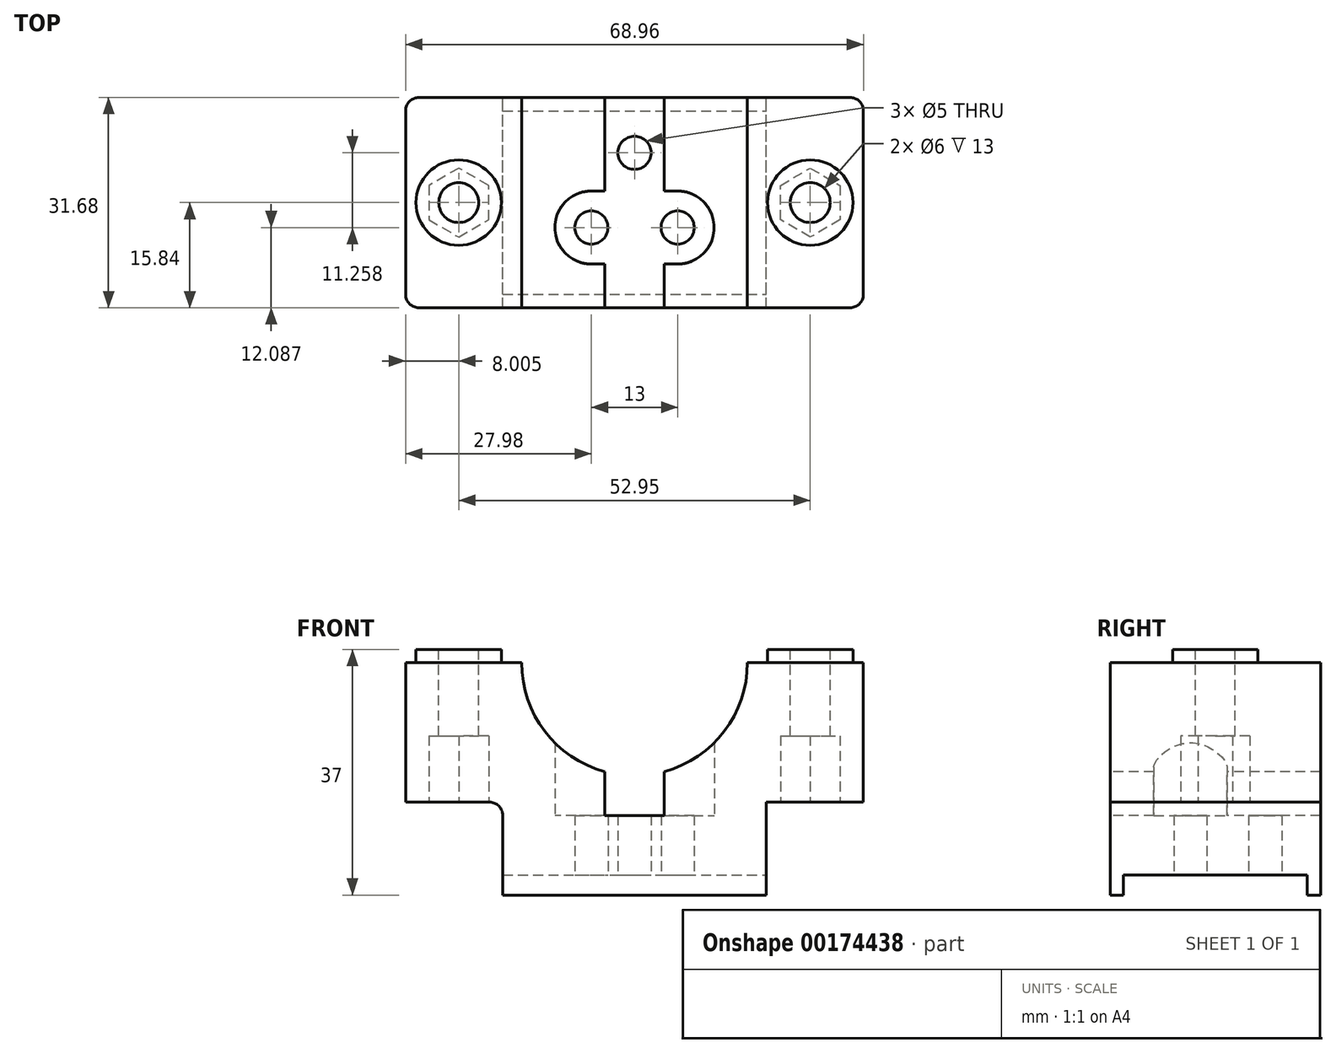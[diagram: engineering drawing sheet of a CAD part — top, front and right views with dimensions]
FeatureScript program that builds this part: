
annotation { "Feature Type Name" : "Feature", "Feature Type Description" : "" }
export const myFeature = defineFeature(function(context is Context, id is Id, definition is map)
    precondition{}
    {
        {
            var Q0;
            Q0=qCreatedBy(makeId("Top.planeOp"),FACE);
            var sketch = newSketch(context, id + "F0", { "sketchPlane" : qUnion([Q0])});
            skLineSegment(sketch, "E0.bottom", {"start": v(34.48, -15.84) * mm, "end": v(-34.48, -15.84) * mm});
            skLineSegment(sketch, "E0.top", {"start": v(34.48, 15.84) * mm, "end": v(-34.48, 15.84) * mm});
            skLineSegment(sketch, "E0.left", {"start": v(34.48, -15.84) * mm, "end": v(34.48, 15.84) * mm});
            skLineSegment(sketch, "E0.right", {"start": v(-34.48, -15.84) * mm, "end": v(-34.48, 15.84) * mm});
            skPoint(sketch, "E0.middle", {"position": v(0, 0) * mm});
            skSolve(sketch);
        }
        {
            var Q0;
            Q0 = qSketchRegion(id + "F0", true);
            extrude(context, id + "F1", {"entities" : qUnion([Q0]), "oppositeDirection" : true, "depth" : 21 * mm});
        }
        {
            var Q0;
            Q0=makeQuery(id+"F1.opExtrude","CAP_FACE",FACE,{"disambiguationData":[OSD([sQuery(id+"F0.wireOp",EDGE,"E0.bottom"),sQuery(id+"F0.wireOp",EDGE,"E0.top"),sQuery(id+"F0.wireOp",EDGE,"E0.left"),sQuery(id+"F0.wireOp",EDGE,"E0.right")])],"isStart":false});
            var sketch = newSketch(context, id + "F2", { "sketchPlane" : qUnion([Q0])});
            skLineSegment(sketch, "E1.bottom", {"start": v(19.85, 15.84) * mm, "end": v(-19.85, 15.84) * mm});
            skLineSegment(sketch, "E1.top", {"start": v(19.85, -15.84) * mm, "end": v(-19.85, -15.84) * mm});
            skLineSegment(sketch, "E1.left", {"start": v(19.85, 15.84) * mm, "end": v(19.85, -15.84) * mm});
            skLineSegment(sketch, "E1.right", {"start": v(-19.85, 15.84) * mm, "end": v(-19.85, -15.84) * mm});
            skPoint(sketch, "E1.middle", {"position": v(0, 0) * mm});
            skSolve(sketch);
        }
        {
            var Q0;
            Q0 = qSketchRegion(id + "F2", true);
            extrude(context, id + "F3", {"entities" : qUnion([Q0]), "operationType" : NewBodyOperationType.ADD, "depth" : 11 * mm});
        }
        {
            var Q0;
            Q0=makeQuery(id+"F1.opExtrude","CAP_FACE",FACE,{"disambiguationData":[OSD([sQuery(id+"F0.wireOp",EDGE,"E0.bottom"),sQuery(id+"F0.wireOp",EDGE,"E0.top"),sQuery(id+"F0.wireOp",EDGE,"E0.left"),sQuery(id+"F0.wireOp",EDGE,"E0.right")])],"isStart":true});
            var sketch = newSketch(context, id + "F4", { "sketchPlane" : qUnion([Q0])});
            skLineSegment(sketch, "E2", {"start": v(-34.48, 0) * mm, "end": v(0, 0) * mm, "construction": true});
            skLineSegment(sketch, "E3", {"start": v(0, 0) * mm, "end": v(0, 15.84) * mm, "construction": true});
            skCircle(sketch, "E4", {"center": v(-26.47, 0) * mm, "radius": 6.43 * mm});
            skCircle(sketch, "E5.MirrorC", {"center": v(26.47, 0) * mm, "radius": 6.43 * mm});
            skLineSegment(sketch, "E6", {"start": v(-32.9, 0) * mm, "end": v(-32.9, -15.84) * mm, "construction": true});
            skCircle(sketch, "E7", {"center": v(-26.47, 0) * mm, "radius": 2.8 * mm});
            skSolve(sketch);
        }
        {
            var Q0;
            Q0 = qSketchRegion(id + "F4", true);
            extrude(context, id + "F5", {"entities" : qUnion([Q0]), "operationType" : NewBodyOperationType.ADD, "depth" : 2 * mm});
        }
        {
            var Q0;
            Q0=makeQuery(id+"F5.opExtrude","CAP_FACE",FACE,{"disambiguationData":[OSD([sQuery(id+"F4.wireOp",EDGE,"E4")])],"isStart":false});
            var sketch = newSketch(context, id + "F6", { "sketchPlane" : qUnion([Q0])});
            skCircle(sketch, "E8", {"center": v(-26.47, 0) * mm, "radius": 3 * mm});
            skLineSegment(sketch, "E9", {"start": v(-26.47, 0) * mm, "end": v(26.47, 0) * mm, "construction": true});
            skLineSegment(sketch, "E10", {"start": v(0, 0) * mm, "end": v(0, 15.84) * mm, "construction": true});
            skCircle(sketch, "E11.MirrorC", {"center": v(26.47, 0) * mm, "radius": 3 * mm});
            skLineSegment(sketch, "E12", {"start": v(-29.47, 0) * mm, "end": v(-29.47, -15.84) * mm, "construction": true});
            skSolve(sketch);
        }
        {
            var Q0;
            Q0 = qSketchRegion(id + "F6", true);
            extrude(context, id + "F7", {"entities" : qUnion([Q0]), "operationType" : NewBodyOperationType.REMOVE, "endBound" : BoundingType.THROUGH_ALL, "oppositeDirection" : true, "depth" : 25 * mm});
        }
        {
            var Q0;
            {var subQ0=sQuery(id+"F0.wireOp",EDGE,"E0.right");var subQ1=sQuery(id+"F0.wireOp",EDGE,"E0.top");var subQ2=sQuery(id+"F0.wireOp",EDGE,"E0.bottom");Q0=makeQuery(id+"F3.boolean.opBoolean","SPLIT",FACE,{"disambiguationData":[TD([makeQuery(id+"F1.opExtrude","SWEPT_FACE",FACE,{"disambiguationData":[OSD([subQ0])]})])],"derivedFrom":makeQuery(id+"F1.opExtrude","CAP_FACE",FACE,{"disambiguationData":[OSD([subQ2,subQ1,sQuery(id+"F0.wireOp",EDGE,"E0.left"),subQ0])],"isStart":false})});}
            var sketch = newSketch(context, id + "F8", { "sketchPlane" : qUnion([Q0])});
            skCircle(sketch, "E13.cCircle", {"center": v(-26.47, 0) * mm, "radius": 4.5 * mm, "construction": true});
            skLineSegment(sketch, "E13.0", {"start": v(-30.97, 2.6) * mm, "end": v(-26.47, 5.2) * mm});
            skLineSegment(sketch, "E13.1", {"start": v(-26.47, 5.2) * mm, "end": v(-21.97, 2.6) * mm});
            skLineSegment(sketch, "E13.2", {"start": v(-21.97, 2.6) * mm, "end": v(-21.97, -2.6) * mm});
            skLineSegment(sketch, "E13.3", {"start": v(-21.97, -2.6) * mm, "end": v(-26.47, -5.2) * mm});
            skLineSegment(sketch, "E13.4", {"start": v(-26.47, -5.2) * mm, "end": v(-30.97, -2.6) * mm});
            skLineSegment(sketch, "E13.5", {"start": v(-30.97, -2.6) * mm, "end": v(-30.97, 2.6) * mm});
            skPoint(sketch, "E13.0.midPoint", {"position": v(-28.73, 3.9) * mm});
            skLineSegment(sketch, "E14", {"start": v(-26.47, 0) * mm, "end": v(-26.47, 5.2) * mm, "construction": true});
            skLineSegment(sketch, "E15", {"start": v(-26.47, 0) * mm, "end": v(0, 0) * mm, "construction": true});
            skLineSegment(sketch, "E16", {"start": v(0, 0) * mm, "end": v(0, 15.84) * mm, "construction": true});
            skLineSegment(sketch, "E17.MirrorCS", {"start": v(30.97, -2.6) * mm, "end": v(30.97, 2.6) * mm});
            skLineSegment(sketch, "E18.MirrorCS", {"start": v(21.97, -2.6) * mm, "end": v(26.47, -5.2) * mm});
            skLineSegment(sketch, "E19.MirrorCS", {"start": v(21.97, 2.6) * mm, "end": v(21.97, -2.6) * mm});
            skLineSegment(sketch, "E20.MirrorCS", {"start": v(30.97, 2.6) * mm, "end": v(26.47, 5.2) * mm});
            skLineSegment(sketch, "E21.MirrorCS", {"start": v(26.47, 0) * mm, "end": v(26.47, 5.2) * mm, "construction": true});
            skLineSegment(sketch, "E22.MirrorCS", {"start": v(26.47, 0) * mm, "end": v(0, 0) * mm, "construction": true});
            skLineSegment(sketch, "E23.MirrorCS", {"start": v(26.48, -5.2) * mm, "end": v(30.98, -2.6) * mm});
            skLineSegment(sketch, "E24.MirrorCS", {"start": v(26.47, 5.2) * mm, "end": v(21.97, 2.6) * mm});
            skPoint(sketch, "E25.MirrorP", {"position": v(28.73, 3.9) * mm});
            skCircle(sketch, "E26.MirrorC", {"center": v(26.47, 0) * mm, "radius": 4.5 * mm, "construction": true});
            skSolve(sketch);
        }
        {
            var Q0;
            Q0 = qSketchRegion(id + "F8", true);
            extrude(context, id + "F9", {"entities" : qUnion([Q0]), "operationType" : NewBodyOperationType.REMOVE, "oppositeDirection" : true, "depth" : 10 * mm});
        }
        {
            var Q0;
            Q0=makeQuery(id+"F3.boolean.opBoolean","MERGE",FACE,{"derivedFrom":[makeQuery(id+"F1.opExtrude","SWEPT_FACE",FACE,{"disambiguationData":[OSD([sQuery(id+"F0.wireOp",EDGE,"E0.bottom")])]}),makeQuery(id+"F3.opExtrude","SWEPT_FACE",FACE,{"disambiguationData":[OSD([sQuery(id+"F2.wireOp",EDGE,"E1.bottom")])]})]});
            var sketch = newSketch(context, id + "F10", { "sketchPlane" : qUnion([Q0])});
            skArc(sketch, "E27", {"start": v(4.5, -16.4) * mm, "mid": v(13.52, -10.3) * mm, "end": v(17, 0) * mm});
            skLineSegment(sketch, "E28.bottom", {"start": v(-4.5, -23) * mm, "end": v(4.5, -23) * mm});
            skLineSegment(sketch, "E28.left", {"start": v(-4.5, -23) * mm, "end": v(-4.5, -16.4) * mm});
            skLineSegment(sketch, "E28.right", {"start": v(4.5, -23) * mm, "end": v(4.5, -16.4) * mm});
            skPoint(sketch, "E28.middle", {"position": v(0, -17) * mm});
            skLineSegment(sketch, "E29", {"start": v(-17, 0) * mm, "end": v(17, 0) * mm});
            skPoint(sketch, "E28.top.start.orphan", {"position": v(-4.5, -11) * mm});
            skPoint(sketch, "E30.orphan", {"position": v(4.5, -11) * mm});
            skArc(sketch, "E31.trimOffspring", {"start": v(-17, 0) * mm, "mid": v(-13.52, -10.3) * mm, "end": v(-4.5, -16.4) * mm});
            skLineSegment(sketch, "E32", {"start": v(0, 0) * mm, "end": v(0, -23) * mm, "construction": true});
            skSolve(sketch);
        }
        {
            var Q0;
            Q0 = qSketchRegion(id + "F10", true);
            extrude(context, id + "F11", {"entities" : qUnion([Q0]), "operationType" : NewBodyOperationType.REMOVE, "endBound" : BoundingType.THROUGH_ALL, "oppositeDirection" : true, "depth" : 25 * mm});
        }
        {
            var Q0;
            Q0=makeQuery(id+"F3.opExtrude","CAP_FACE",FACE,{"disambiguationData":[OSD([sQuery(id+"F2.wireOp",EDGE,"E1.bottom"),sQuery(id+"F2.wireOp",EDGE,"E1.top"),sQuery(id+"F2.wireOp",EDGE,"E1.left"),sQuery(id+"F2.wireOp",EDGE,"E1.right")])],"isStart":false});
            var sketch = newSketch(context, id + "F12", { "sketchPlane" : qUnion([Q0])});
            skLineSegment(sketch, "E33.bottom", {"start": v(-19.85, 15.84) * mm, "end": v(19.85, 15.84) * mm});
            skLineSegment(sketch, "E33.top", {"start": v(-19.85, 13.84) * mm, "end": v(19.85, 13.84) * mm});
            skLineSegment(sketch, "E33.left", {"start": v(-19.85, 15.84) * mm, "end": v(-19.85, 13.84) * mm});
            skLineSegment(sketch, "E33.right", {"start": v(19.85, 15.84) * mm, "end": v(19.85, 13.84) * mm});
            skLineSegment(sketch, "E34", {"start": v(-19.85, 0) * mm, "end": v(0, 0) * mm, "construction": true});
            skLineSegment(sketch, "E35", {"start": v(0, 0) * mm, "end": v(0, 15.84) * mm, "construction": true});
            skLineSegment(sketch, "E36.MirrorCS", {"start": v(19.85, -15.84) * mm, "end": v(19.85, -13.84) * mm});
            skLineSegment(sketch, "E37.MirrorCS", {"start": v(-19.85, -15.84) * mm, "end": v(-19.85, -13.84) * mm});
            skLineSegment(sketch, "E38.MirrorCS", {"start": v(-19.85, -13.84) * mm, "end": v(19.85, -13.84) * mm});
            skLineSegment(sketch, "E39.MirrorCS", {"start": v(-19.85, -15.84) * mm, "end": v(19.85, -15.84) * mm});
            skSolve(sketch);
        }
        {
            var Q0;
            Q0=makeQuery(id+"F12.imprint","IMPRINT",FACE,{"disambiguationData":[TD([[makeQuery(id+"F12.imprint","IMPRINT",EDGE,{"derivedFrom":sQuery(id+"F12.wireOp",EDGE,"E33.bottom")}),1.0]])]});
            var Q1;
            Q1=makeQuery(id+"F12.imprint","IMPRINT",FACE,{"disambiguationData":[TD([[makeQuery(id+"F12.imprint","IMPRINT",EDGE,{"derivedFrom":sQuery(id+"F12.wireOp",EDGE,"E36.MirrorCS")}),-1.0]])]});
            extrude(context, id + "F13", {"entities" : qUnion([Q0, Q1]), "operationType" : NewBodyOperationType.ADD, "depth" : 3 * mm});
        }
        {
            var Q0;
            Q0=makeQuery(id+"F3.opExtrude","CAP_FACE",FACE,{"disambiguationData":[OSD([sQuery(id+"F2.wireOp",EDGE,"E1.bottom"),sQuery(id+"F2.wireOp",EDGE,"E1.top"),sQuery(id+"F2.wireOp",EDGE,"E1.left"),sQuery(id+"F2.wireOp",EDGE,"E1.right")])],"isStart":false});
            var sketch = newSketch(context, id + "F14", { "sketchPlane" : qUnion([Q0])});
            skCircle(sketch, "E40.cCircle", {"center": v(0, 0) * mm, "radius": 3.75 * mm, "construction": true});
            skLineSegment(sketch, "E40.0", {"start": v(-6.5, 3.75) * mm, "end": v(6.5, 3.75) * mm, "construction": true});
            skLineSegment(sketch, "E40.1", {"start": v(6.5, 3.75) * mm, "end": v(0, -7.5) * mm, "construction": true});
            skLineSegment(sketch, "E40.2", {"start": v(0, -7.5) * mm, "end": v(-6.5, 3.75) * mm, "construction": true});
            skPoint(sketch, "E40.0.midPoint", {"position": v(0, 3.75) * mm});
            skCircle(sketch, "E41", {"center": v(-6.5, 3.75) * mm, "radius": 2.5 * mm});
            skCircle(sketch, "E42", {"center": v(6.5, 3.75) * mm, "radius": 2.5 * mm});
            skCircle(sketch, "E43", {"center": v(0, -7.5) * mm, "radius": 2.5 * mm});
            skLineSegment(sketch, "E44.top", {"start": v(-4, 3.75) * mm, "end": v(4, 3.75) * mm, "construction": true});
            skSolve(sketch);
        }
        {
            var Q0;
            Q0=makeQuery(id+"F14.imprint","IMPRINT",FACE,{"disambiguationData":[TD([[makeQuery(id+"F14.imprint","IMPRINT",EDGE,{"derivedFrom":sQuery(id+"F14.wireOp",EDGE,"E41")}),1.0]])]});
            var Q1;
            Q1=makeQuery(id+"F14.imprint","IMPRINT",FACE,{"disambiguationData":[TD([[makeQuery(id+"F14.imprint","IMPRINT",EDGE,{"derivedFrom":sQuery(id+"F14.wireOp",EDGE,"E42")}),1.0]])]});
            var Q2;
            Q2=makeQuery(id+"F14.imprint","IMPRINT",FACE,{"disambiguationData":[TD([[makeQuery(id+"F14.imprint","IMPRINT",EDGE,{"derivedFrom":sQuery(id+"F14.wireOp",EDGE,"E43")}),1.0]])]});
            extrude(context, id + "F15", {"entities" : qUnion([Q0, Q1, Q2]), "operationType" : NewBodyOperationType.REMOVE, "endBound" : BoundingType.THROUGH_ALL, "oppositeDirection" : true, "depth" : 25 * mm});
        }
        {
            var Q0;
            Q0=makeQuery(id+"F11.boolean.opBoolean","COPY",FACE,{"derivedFrom":makeQuery(id+"F11.opExtrude","SWEPT_FACE",FACE,{"disambiguationData":[OSD([sQuery(id+"F10.wireOp",EDGE,"E28.bottom")])]})});
            var sketch = newSketch(context, id + "F16", { "sketchPlane" : qUnion([Q0])});
            skLineSegment(sketch, "E45", {"start": v(-6.5, -3.75) * mm, "end": v(6.5, -3.75) * mm, "construction": true});
            skArc(sketch, "E46.0.startCap", {"start": v(-6.5, -9.25) * mm, "mid": v(-12, -3.75) * mm, "end": v(-6.5, 1.75) * mm});
            skArc(sketch, "E46.0.endCap", {"start": v(6.5, 1.75) * mm, "mid": v(12, -3.75) * mm, "end": v(6.5, -9.25) * mm});
            skLineSegment(sketch, "E46.0.left", {"start": v(-6.5, 1.75) * mm, "end": v(6.5, 1.75) * mm});
            skLineSegment(sketch, "E46.0.right", {"start": v(-6.5, -9.25) * mm, "end": v(6.5, -9.25) * mm});
            skSolve(sketch);
        }
        {
            var Q0;
            Q0 = qSketchRegion(id + "F16", true);
            extrude(context, id + "F17", {"entities" : qUnion([Q0]), "operationType" : NewBodyOperationType.REMOVE, "endBound" : BoundingType.THROUGH_ALL, "depth" : 25 * mm});
        }
        {
            var Q0;
            Q0=makeQuery(id+"F1.opExtrude","SWEPT_EDGE",EDGE,{"disambiguationData":[OSD([sQuery(id+"F0.wireOp",EDGE,"E0.bottom"),sQuery(id+"F0.wireOp",EDGE,"E0.right")])]});
            var Q1;
            Q1=makeQuery(id+"F1.opExtrude","SWEPT_EDGE",EDGE,{"disambiguationData":[OSD([sQuery(id+"F0.wireOp",EDGE,"E0.bottom"),sQuery(id+"F0.wireOp",EDGE,"E0.left")])]});
            var Q2;
            Q2=makeQuery(id+"F1.opExtrude","SWEPT_EDGE",EDGE,{"disambiguationData":[OSD([sQuery(id+"F0.wireOp",EDGE,"E0.top"),sQuery(id+"F0.wireOp",EDGE,"E0.left")])]});
            var Q3;
            Q3=makeQuery(id+"F1.opExtrude","SWEPT_EDGE",EDGE,{"disambiguationData":[OSD([sQuery(id+"F0.wireOp",EDGE,"E0.top"),sQuery(id+"F0.wireOp",EDGE,"E0.right")])]});
            fillet(context, id + "F18", {"entities" : qUnion([Q0, Q1, Q2, Q3]), "radius" : 2 * mm, "tangentPropagation" : true, "allowEdgeOverflow" : false});
        }
        {
            var Q0;
            Q0=makeQuery(id+"F3.opExtrude","CAP_EDGE",EDGE,{"disambiguationData":[OSD([sQuery(id+"F2.wireOp",EDGE,"E1.right")])],"isStart":true});
            var Q1;
            Q1=makeQuery(id+"F3.opExtrude","CAP_EDGE",EDGE,{"disambiguationData":[OSD([sQuery(id+"F2.wireOp",EDGE,"E1.left")])],"isStart":true});
            fillet(context, id + "F19", {"entities" : qUnion([Q0, Q1]), "radius" : 2 * mm, "tangentPropagation" : true, "allowEdgeOverflow" : false});
        }
    });
